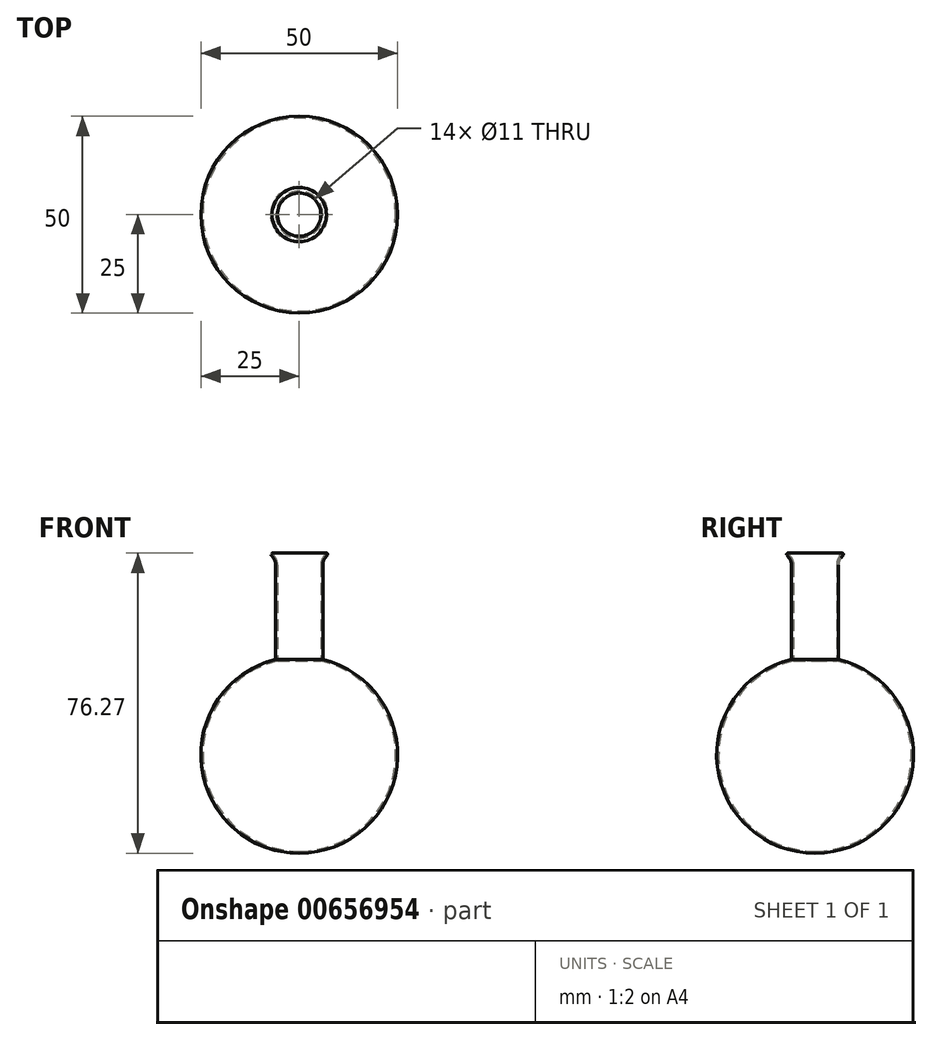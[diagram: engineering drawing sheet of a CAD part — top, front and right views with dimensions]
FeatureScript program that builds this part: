
annotation { "Feature Type Name" : "Feature", "Feature Type Description" : "" }
export const myFeature = defineFeature(function(context is Context, id is Id, definition is map)
    precondition{}
    {
        {
            var Q0;
            Q0=qCreatedBy(makeId("Front.planeOp"),FACE);
            var sketch = newSketch(context, id + "F0", { "sketchPlane" : qUnion([Q0])});
            skArc(sketch, "E0", {"start": v(-6, 24.27) * mm, "mid": v(-24.82, -3.02) * mm, "end": v(0, -25) * mm});
            skLineSegment(sketch, "E1", {"start": v(0, -44.9) * mm, "end": v(0, 62.29) * mm, "construction": true});
            skLineSegment(sketch, "E2", {"start": v(-6, 24.27) * mm, "end": v(-6, 48.26) * mm});
            skLineSegment(sketch, "E3", {"start": v(-6.61, 50.07) * mm, "end": v(-7.15, 50.79) * mm});
            skLineSegment(sketch, "E4", {"start": v(-6.91, 51.27) * mm, "end": v(0, 51.27) * mm});
            skPoint(sketch, "E5.visualSharp", {"position": v(-7.52, 51.27) * mm});
            skArc(sketch, "E5.filletArc", {"start": v(-6.91, 51.27) * mm, "mid": v(-7.18, 51.1) * mm, "end": v(-7.15, 50.79) * mm});
            skPoint(sketch, "E6.visualSharp", {"position": v(-6, 49.27) * mm});
            skArc(sketch, "E6.filletArc", {"start": v(-6, 48.26) * mm, "mid": v(-6.16, 49.22) * mm, "end": v(-6.61, 50.07) * mm});
            skLineSegment(sketch, "E7", {"start": v(0, -25) * mm, "end": v(0, 51.27) * mm});
            skSolve(sketch);
        }
        {
            var Q0;
            Q0=makeQuery(id+"F0.imprint","IMPRINT",FACE,{"disambiguationData":[TD([[makeQuery(id+"F0.imprint","IMPRINT",EDGE,{"derivedFrom":sQuery(id+"F0.wireOp",EDGE,"E0")}),1.0]])]});
            var Q1;
            Q1=sQuery(id+"F0.wireOp",EDGE,"E1");
            revolve(context, id + "F1", {"entities" : qUnion([Q0]), "axis" : qUnion([Q1]), "revolveType" : RevolveType.FULL});
        }
        {
            var Q0;
            Q0=makeQuery(id+"F1.opRevolve","SWEPT_FACE",FACE,{"disambiguationData":[OSD([sQuery(id+"F0.wireOp",EDGE,"E4")])]});
            shell(context, id + "F2", {"entities" : qUnion([Q0]), "thickness" : 0.5 * mm});
        }
    });
